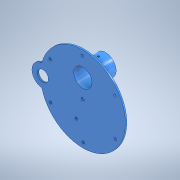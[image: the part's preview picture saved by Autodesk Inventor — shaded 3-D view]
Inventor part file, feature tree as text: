
AUTODESK INVENTOR PART (.ipt)
format: ipt  version: 2022.2 (Build 262287000, 287)  size: 408,576 bytes
history: native  units: in
note: dims shown in document units (in); Inventor stores cm internally (conversion verified against a paired STEP export)
features: sketch x10, extrude x6, hole x5, plane x1, pattern_circular x1
ambient origin geometry x8: Origin, YZ Plane, XZ Plane, XY Plane, X Axis, Y Axis, Z Axis, Center Point
bodies: Solid3 (feature_tree)
feature tree (23):
  extrude  "Extrusion4"  Depth=0.1in TaperAngle=0.0deg
  extrude  "Extrusion5"  Depth=1.29in
  extrude  "DescriptionText"  Depth=0.025in TaperAngle=0.0deg
  extrude  "EyepieceHolder"  Depth=1.5in TaperAngle=0.0deg
  hole  "Hole1"  [1 undecoded]
  extrude  "Extrusion8"  TaperAngle=0.0deg  [1 undecoded]
  extrude  "Extrusion9"  Depth=0.1in
  hole  "Hole2"  [1 undecoded]
  hole  "MountingHoleSize8"  [1 undecoded]
  hole  "Hole4"  [1 undecoded]
  plane  "Work Plane1"
  hole  "ThreadHoleInEyepieceInsert"  [1 undecoded]
  pattern_circular  "Circular PatternForEyepieceScrew"  [2 undecoded]
  sketch  "Sketch7"  dims[d15=6.0in d16=0.1in d17=0.0in]
  sketch  "Sketch8"  dims[d18=1.3057in d19=1.29in]
  sketch  "Sketch9"  dims[d20=0.0in d21=0.0in d22=0.025in d23=0.0in]
  sketch  "Sketch10"  dims[d24=0.1in d25=1.5in d26=0.0in]
  sketch  "Sketch11"  dims[d27=0.201in d28=0.75in d29=0.385in d30=0.25in d31=0.5635in d32=0.375in d33=0.0in d34=0.25in]
  sketch  "Sketch12"  dims[d35=2.825in d36=0.0in d37=0.0in]
  sketch  "Sketch13"  dims[d38=0.6721in d39=0.1in]
  sketch  "Sketch14"  dims[d40=1.0in d41=0.0in d42=3.0in]
  sketch  "Sketch15"  dims[d43=0.1237in]
  sketch  "Sketch16"  dims[d44=0.177in d45=0.75in d46=0.375in d47=0.25in d48=0.5635in d49=1.0in d50=0.8108in d51=5.2762in d52=60.0deg d53=2.3622in d55=360.0deg d57=0.177in d58=0.75in d59=0.75in d60=0.188in d61=0.5635in d62=0.375in d63=0.0in d64=2.825in d65=0.77in d66=0.75in d67=0.27in d68=0.08in d69=0.5635in d70=1.0in d71=0.8108in d72=0.13in d73=0.328in d74=0.332in d75=0.25in d76=0.5635in d77=1.0in d78=0.0in d79=1.1811in d80=360.0deg d82=1.0in]
note: 8 required parameter values undecoded (feature->parameter linkage not recoverable at this tier; creation-order binding heuristic only, values carry confidence <= 0.55)
